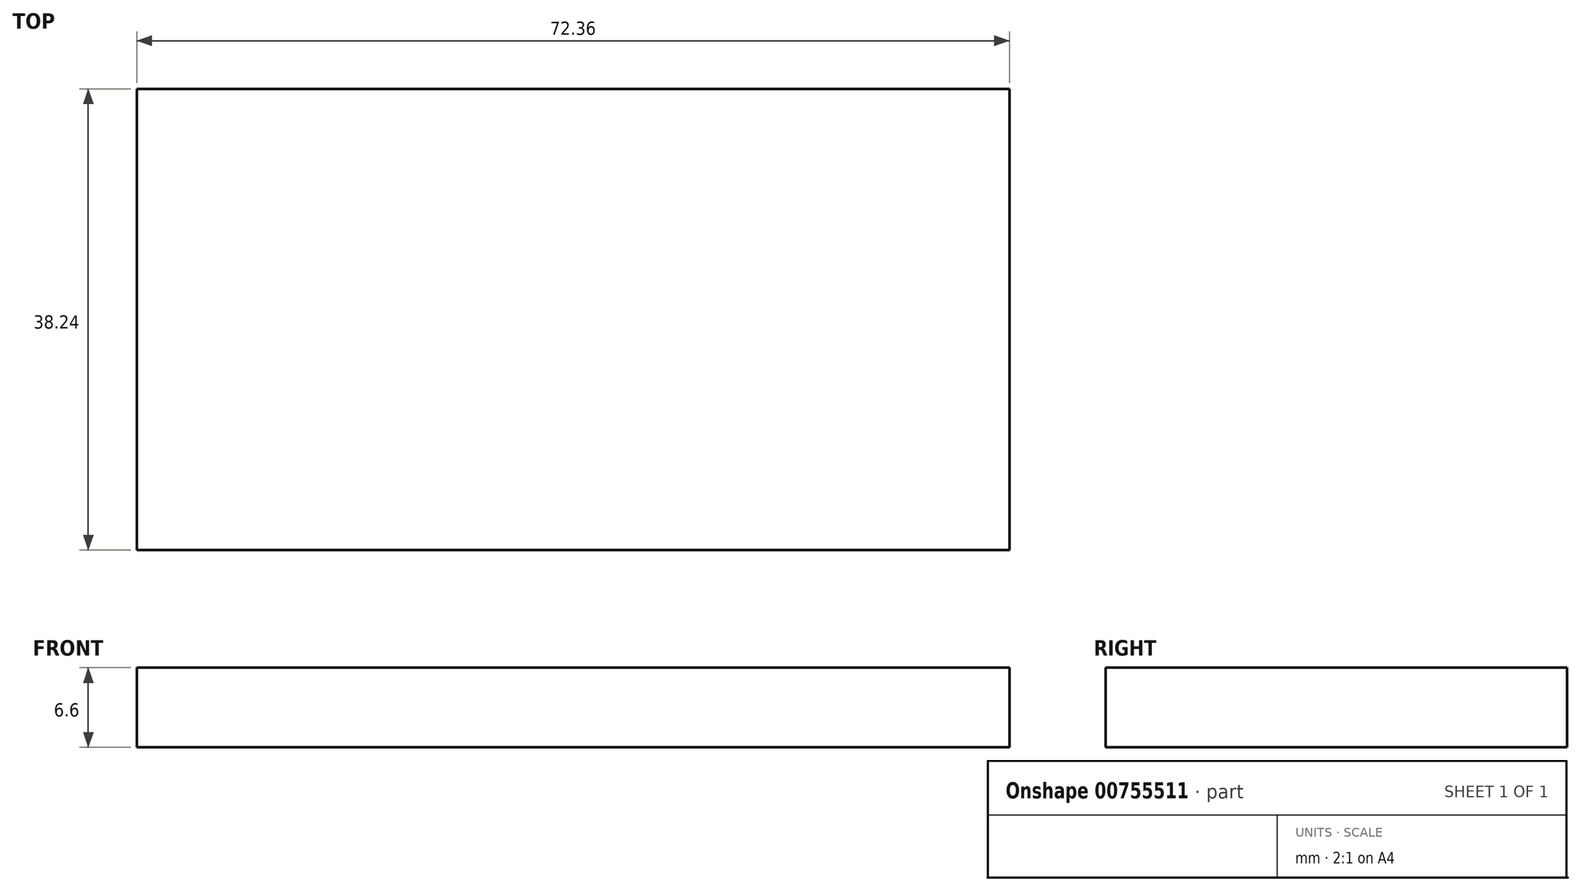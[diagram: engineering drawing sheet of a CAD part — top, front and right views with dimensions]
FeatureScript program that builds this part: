
annotation { "Feature Type Name" : "Feature", "Feature Type Description" : "" }
export const myFeature = defineFeature(function(context is Context, id is Id, definition is map)
    precondition{}
    {
        {
            var Q0;
            Q0=qCreatedBy(makeId("Top.planeOp"),FACE);
            var sketch = newSketch(context, id + "F0", { "sketchPlane" : qUnion([Q0])});
            skLineSegment(sketch, "E0.bottom", {"start": v(34.02, -18.35) * mm, "end": v(-38.34, -18.35) * mm});
            skLineSegment(sketch, "E0.top", {"start": v(34.02, 19.9) * mm, "end": v(-38.34, 19.9) * mm});
            skLineSegment(sketch, "E0.left", {"start": v(34.02, -18.35) * mm, "end": v(34.02, 19.9) * mm});
            skLineSegment(sketch, "E0.right", {"start": v(-38.34, -18.35) * mm, "end": v(-38.34, 19.9) * mm});
            skPoint(sketch, "E0.middle", {"position": v(-2.16, 0.77) * mm});
            skCircle(sketch, "E1", {"center": v(-6.46, 5.13) * mm, "radius": 8.34 * mm});
            skCircle(sketch, "E2", {"center": v(-6.46, 5.13) * mm, "radius": 4.48 * mm});
            skSolve(sketch);
        }
        {
            var Q0;
            Q0=makeQuery(id+"F0.imprint","IMPRINT",FACE,{"disambiguationData":[TD([[makeQuery(id+"F0.imprint","IMPRINT",EDGE,{"derivedFrom":sQuery(id+"F0.wireOp",EDGE,"E2")}),1.0]])]});
            var Q1;
            Q1=makeQuery(id+"F0.imprint","IMPRINT",FACE,{"disambiguationData":[TD([[makeQuery(id+"F0.imprint","IMPRINT",EDGE,{"derivedFrom":sQuery(id+"F0.wireOp",EDGE,"E1")}),1.0]])]});
            var Q2;
            Q2=makeQuery(id+"F0.imprint","IMPRINT",FACE,{"disambiguationData":[TD([[makeQuery(id+"F0.imprint","IMPRINT",EDGE,{"derivedFrom":sQuery(id+"F0.wireOp",EDGE,"E0.bottom")}),-1.0]])]});
            extrude(context, id + "F1", {"entities" : qUnion([Q0, Q1, Q2]), "oppositeDirection" : true, "depth" : 6.6 * mm, "offsetDistance" : 25 * mm});
        }
    });
